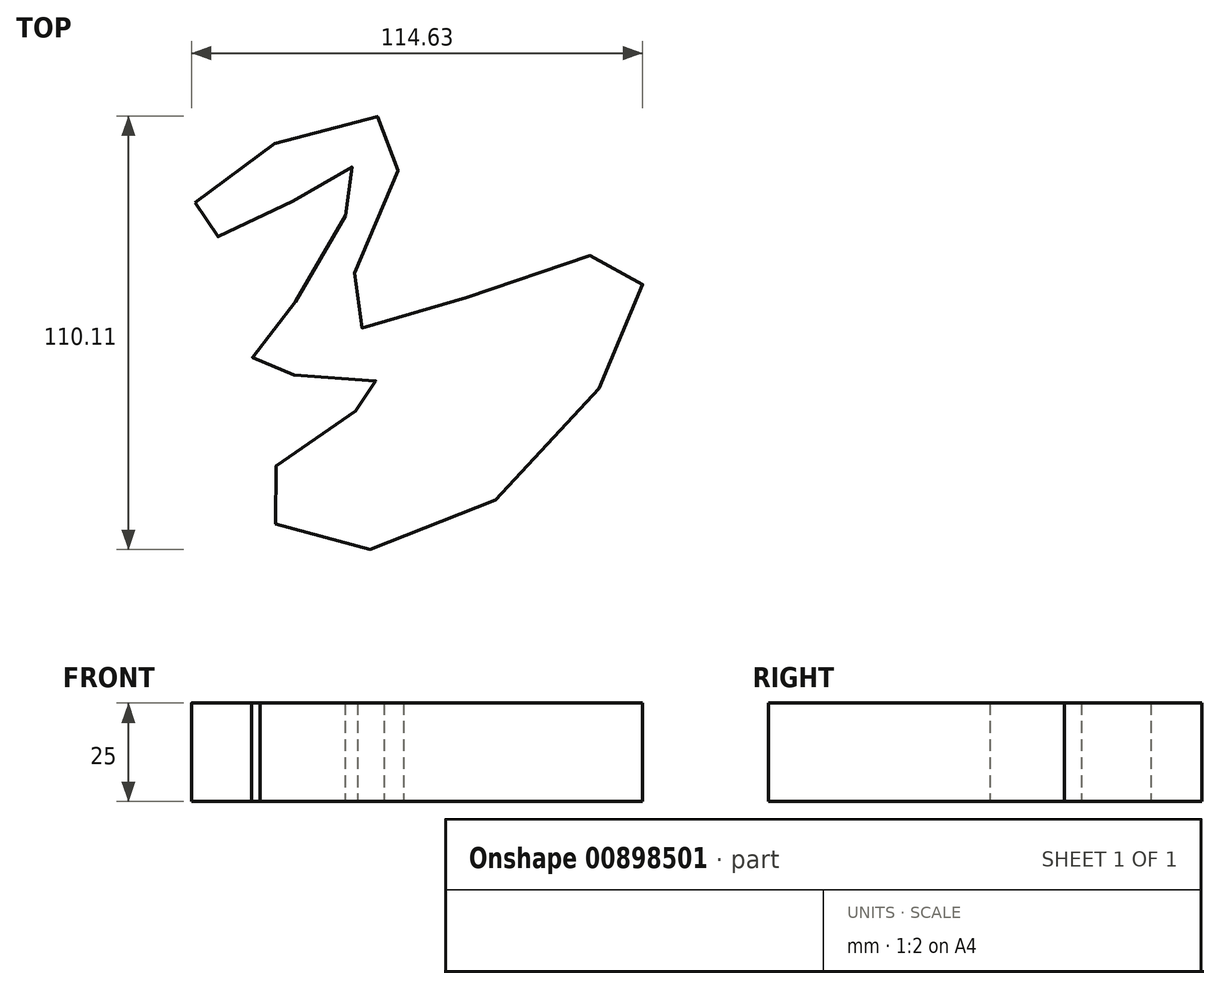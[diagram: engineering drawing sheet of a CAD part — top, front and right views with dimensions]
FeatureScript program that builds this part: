
annotation { "Feature Type Name" : "Feature", "Feature Type Description" : "" }
export const myFeature = defineFeature(function(context is Context, id is Id, definition is map)
    precondition{}
    {
        {
            var Q0;
            Q0=qCreatedBy(makeId("Top.planeOp"),FACE);
            var sketch = newSketch(context, id + "F0", { "sketchPlane" : qUnion([Q0])});
            skFitSpline(sketch, "E0", {"points": [v(-66.13, 39.87) * mm, v(-14.12, 59.12) * mm, v(-27.13, 9.37) * mm, v(44.13, 26.12) * mm, v(-5.38, -44.63) * mm, v(-49.13, -32.13) * mm, v(-18.13, -6.63) * mm, v(-50.38, -2.38) * mm, v(-41.38, 13.62) * mm, v(-25.88, 48.87) * mm, v(-59.13, 31.37) * mm, v(-66.13, 39.87) * mm]});
            skSolve(sketch);
        }
        {
            var Q0;
            Q0=makeQuery(id+"F0.imprint","IMPRINT",FACE,{"disambiguationData":[TD([[makeQuery(id+"F0.imprint","IMPRINT",EDGE,{"derivedFrom":sQuery(id+"F0.wireOp",EDGE,"E0")}),-1.0]])]});
            extrude(context, id + "F1", {"entities" : qUnion([Q0]), "depth" : 25 * mm, "offsetDistance" : 25 * mm});
        }
    });
